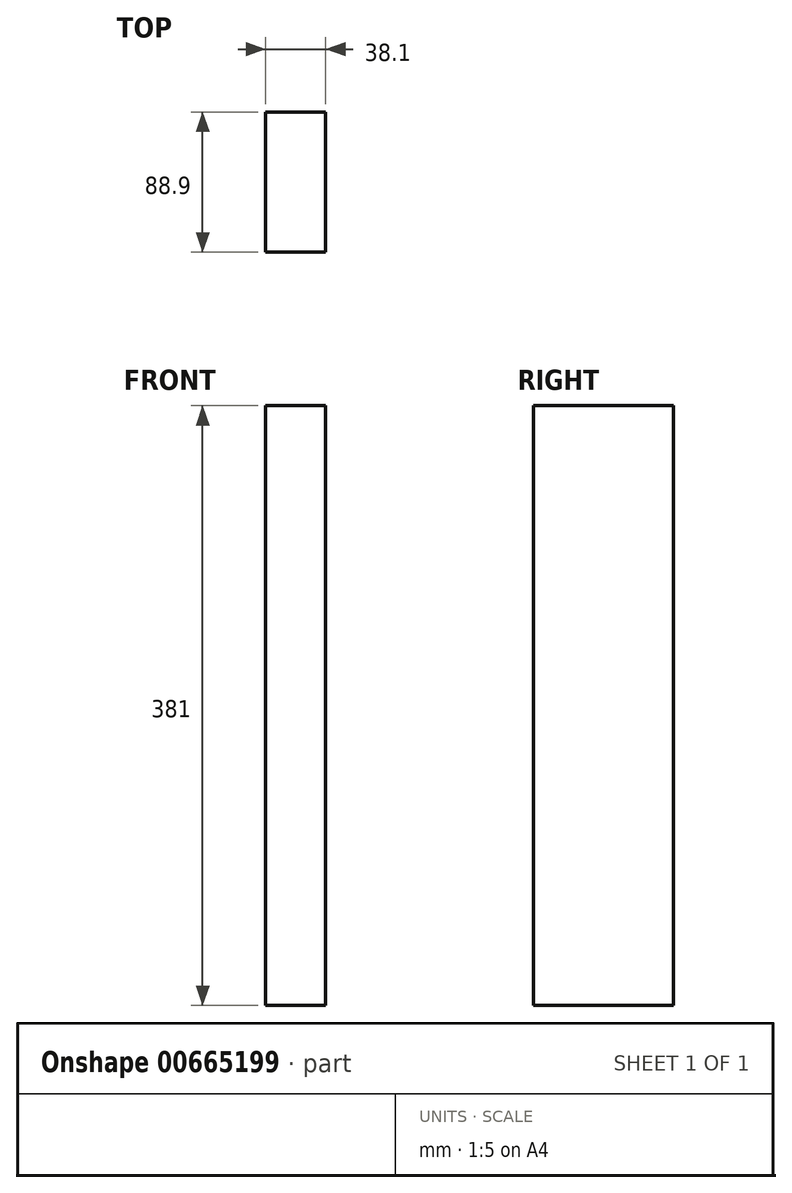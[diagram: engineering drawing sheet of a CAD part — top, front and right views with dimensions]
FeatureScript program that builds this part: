
annotation { "Feature Type Name" : "Feature", "Feature Type Description" : "" }
export const myFeature = defineFeature(function(context is Context, id is Id, definition is map)
    precondition{}
    {
        {
            var Q0;
            Q0=qCreatedBy(makeId("Top.planeOp"),FACE);
            var sketch = newSketch(context, id + "F0", { "sketchPlane" : qUnion([Q0])});
            skLineSegment(sketch, "E0.bottom", {"start": v(19.05, -44.45) * mm, "end": v(-19.05, -44.45) * mm});
            skLineSegment(sketch, "E0.top", {"start": v(19.05, 44.45) * mm, "end": v(-19.05, 44.45) * mm});
            skLineSegment(sketch, "E0.left", {"start": v(19.05, -44.45) * mm, "end": v(19.05, 44.45) * mm});
            skLineSegment(sketch, "E0.right", {"start": v(-19.05, -44.45) * mm, "end": v(-19.05, 44.45) * mm});
            skPoint(sketch, "E0.middle", {"position": v(0, 0) * mm});
            skSolve(sketch);
        }
        {
            var Q0;
            Q0=makeQuery(id+"F0.imprint","IMPRINT",FACE,{"disambiguationData":[TD([[makeQuery(id+"F0.imprint","IMPRINT",EDGE,{"derivedFrom":sQuery(id+"F0.wireOp",EDGE,"E0.bottom")}),-1.0]])]});
            extrude(context, id + "F1", {"entities" : qUnion([Q0]), "depth" : 381 * mm, "offsetDistance" : 25.4 * mm});
        }
    });
